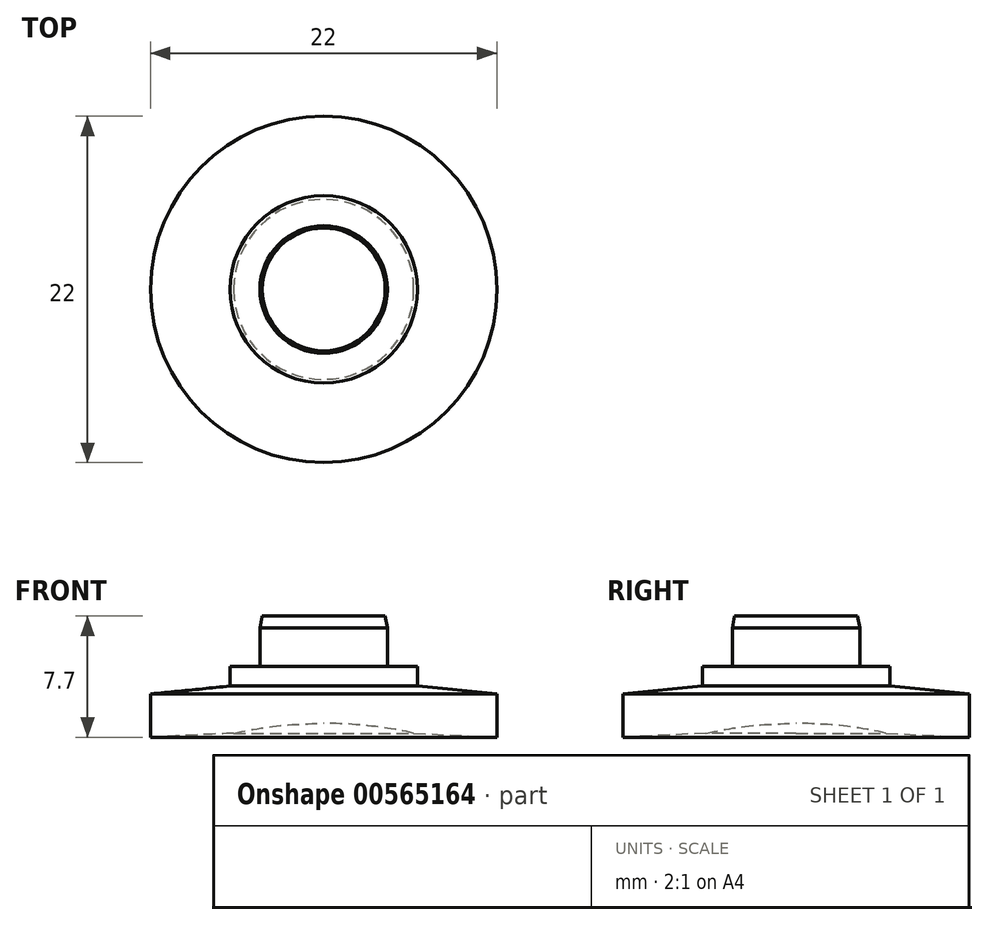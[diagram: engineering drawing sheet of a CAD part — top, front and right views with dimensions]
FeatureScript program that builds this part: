
annotation { "Feature Type Name" : "Feature", "Feature Type Description" : "" }
export const myFeature = defineFeature(function(context is Context, id is Id, definition is map)
    precondition{}
    {
        {
            var Q0;
            Q0=qCreatedBy(makeId("Front.planeOp"),FACE);
            var sketch = newSketch(context, id + "F0", { "sketchPlane" : qUnion([Q0])});
            skLineSegment(sketch, "E0", {"start": v(0, 7.7) * mm, "end": v(3.9, 7.7) * mm});
            skLineSegment(sketch, "E1", {"start": v(4.05, 6.95) * mm, "end": v(4.05, 4.5) * mm});
            skLineSegment(sketch, "E2", {"start": v(4.05, 4.5) * mm, "end": v(5.95, 4.5) * mm});
            skLineSegment(sketch, "E3", {"start": v(5.95, 4.5) * mm, "end": v(5.95, 3.25) * mm});
            skLineSegment(sketch, "E4", {"start": v(11, 2.75) * mm, "end": v(11, 0) * mm});
            skPoint(sketch, "E5.orphan", {"position": v(0, 6.86) * mm});
            skLineSegment(sketch, "E6", {"start": v(11, 0) * mm, "end": v(5.72, 0.26) * mm});
            skLineSegment(sketch, "E7", {"start": v(0, 0.88) * mm, "end": v(0, 7.7) * mm});
            skEllipticalArc(sketch, "E8", {});
            skLineSegment(sketch, "E9", {"start": v(3.9, 7.7) * mm, "end": v(4.05, 6.95) * mm});
            skPoint(sketch, "E10.orphan", {"position": v(4.05, 7.7) * mm});
            skLineSegment(sketch, "E11", {"start": v(5.95, 3.25) * mm, "end": v(11, 2.75) * mm});
            const initialGuessF0  = {"E8": [0, -0.0060900067910552025, 1, 0, 0.013899165205657482, 0.006967667306746596, 1.1467714955425703, 1.5707963267948966]};
            skSetInitialGuess(sketch, initialGuessF0);
            skSolve(sketch);
        }
        {
            var Q0;
            Q0 = qSketchRegion(id + "F0", true);
            var Q1;
            Q1=sQuery(id+"F0.wireOp",EDGE,"E7");
            revolve(context, id + "F1", {"entities" : qUnion([Q0]), "axis" : qUnion([Q1]), "revolveType" : RevolveType.FULL});
        }
    });
